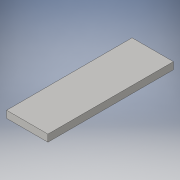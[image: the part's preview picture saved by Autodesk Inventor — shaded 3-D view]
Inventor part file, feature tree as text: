
AUTODESK INVENTOR PART (.ipt)
format: ipt  version: 2016 (Build 200138000, 138)  size: 86,528 bytes
history: native  units: in
note: dims shown in document units (in); Inventor stores cm internally (conversion verified against a paired STEP export)
features: extrude x1, sketch x1
ambient origin geometry x8: Origin, YZ Plane, XZ Plane, XY Plane, X Axis, Y Axis, Z Axis, Center Point
bodies: Solid1 (feature_tree)
feature tree (2):
  extrude  "Extrusion1"  Depth=6.6in
  sketch  "Sketch1"  dims[d0=2.174in d1=6.6in d2=0.3701in d3=0.0in]
